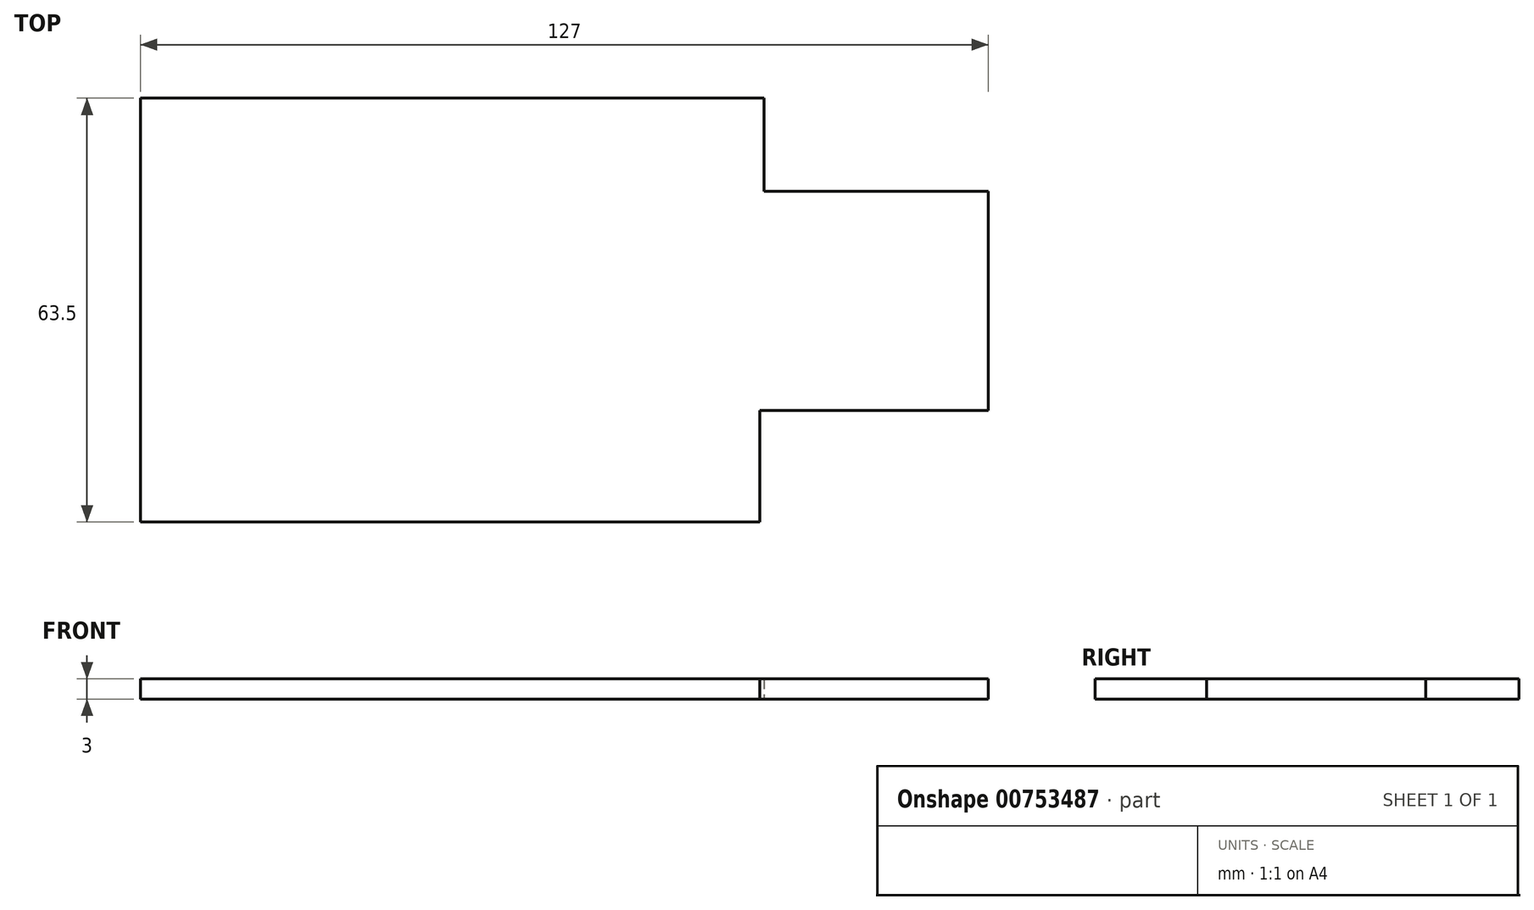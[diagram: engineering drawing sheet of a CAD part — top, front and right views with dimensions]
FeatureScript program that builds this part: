
annotation { "Feature Type Name" : "Feature", "Feature Type Description" : "" }
export const myFeature = defineFeature(function(context is Context, id is Id, definition is map)
    precondition{}
    {
        {
            var Q0;
            Q0=qCreatedBy(makeId("Top.planeOp"),FACE);
            var sketch = newSketch(context, id + "F0", { "sketchPlane" : qUnion([Q0])});
            skLineSegment(sketch, "E0.bottom", {"start": v(63.5, 31.75) * mm, "end": v(-63.5, 31.75) * mm});
            skLineSegment(sketch, "E0.top", {"start": v(63.5, -31.75) * mm, "end": v(-63.5, -31.75) * mm});
            skLineSegment(sketch, "E0.left", {"start": v(63.5, 31.75) * mm, "end": v(63.5, -31.75) * mm});
            skLineSegment(sketch, "E0.right", {"start": v(-63.5, 31.75) * mm, "end": v(-63.5, -31.75) * mm});
            skPoint(sketch, "E0.middle", {"position": v(0, 0) * mm});
            skLineSegment(sketch, "E1.bottom", {"start": v(29.92, 31.75) * mm, "end": v(63.5, 31.75) * mm});
            skLineSegment(sketch, "E1.top", {"start": v(29.92, 17.78) * mm, "end": v(63.5, 17.78) * mm});
            skLineSegment(sketch, "E1.left", {"start": v(29.92, 31.75) * mm, "end": v(29.92, 17.78) * mm});
            skLineSegment(sketch, "E1.right", {"start": v(63.5, 31.75) * mm, "end": v(63.5, 17.78) * mm});
            skLineSegment(sketch, "E2.bottom", {"start": v(63.5, -31.75) * mm, "end": v(29.26, -31.75) * mm});
            skLineSegment(sketch, "E2.top", {"start": v(63.5, -15.03) * mm, "end": v(29.26, -15.03) * mm});
            skLineSegment(sketch, "E2.left", {"start": v(63.5, -31.75) * mm, "end": v(63.5, -15.03) * mm});
            skLineSegment(sketch, "E2.right", {"start": v(29.26, -31.75) * mm, "end": v(29.26, -15.03) * mm});
            skSolve(sketch);
        }
        {
            var Q0;
            {var subQ3=sQuery(id+"F0.wireOp",EDGE,"E0.right");Q0=makeQuery(id+"F0.imprint","IMPRINT",FACE,{"disambiguationData":[TD([[makeQuery(id+"F0.imprint","IMPRINT",EDGE,{"derivedFrom":subQ3}),1.0]])]});}
            extrude(context, id + "F1", {"entities" : qUnion([Q0]), "depth" : 3 * mm, "offsetDistance" : 25.4 * mm});
        }
    });
